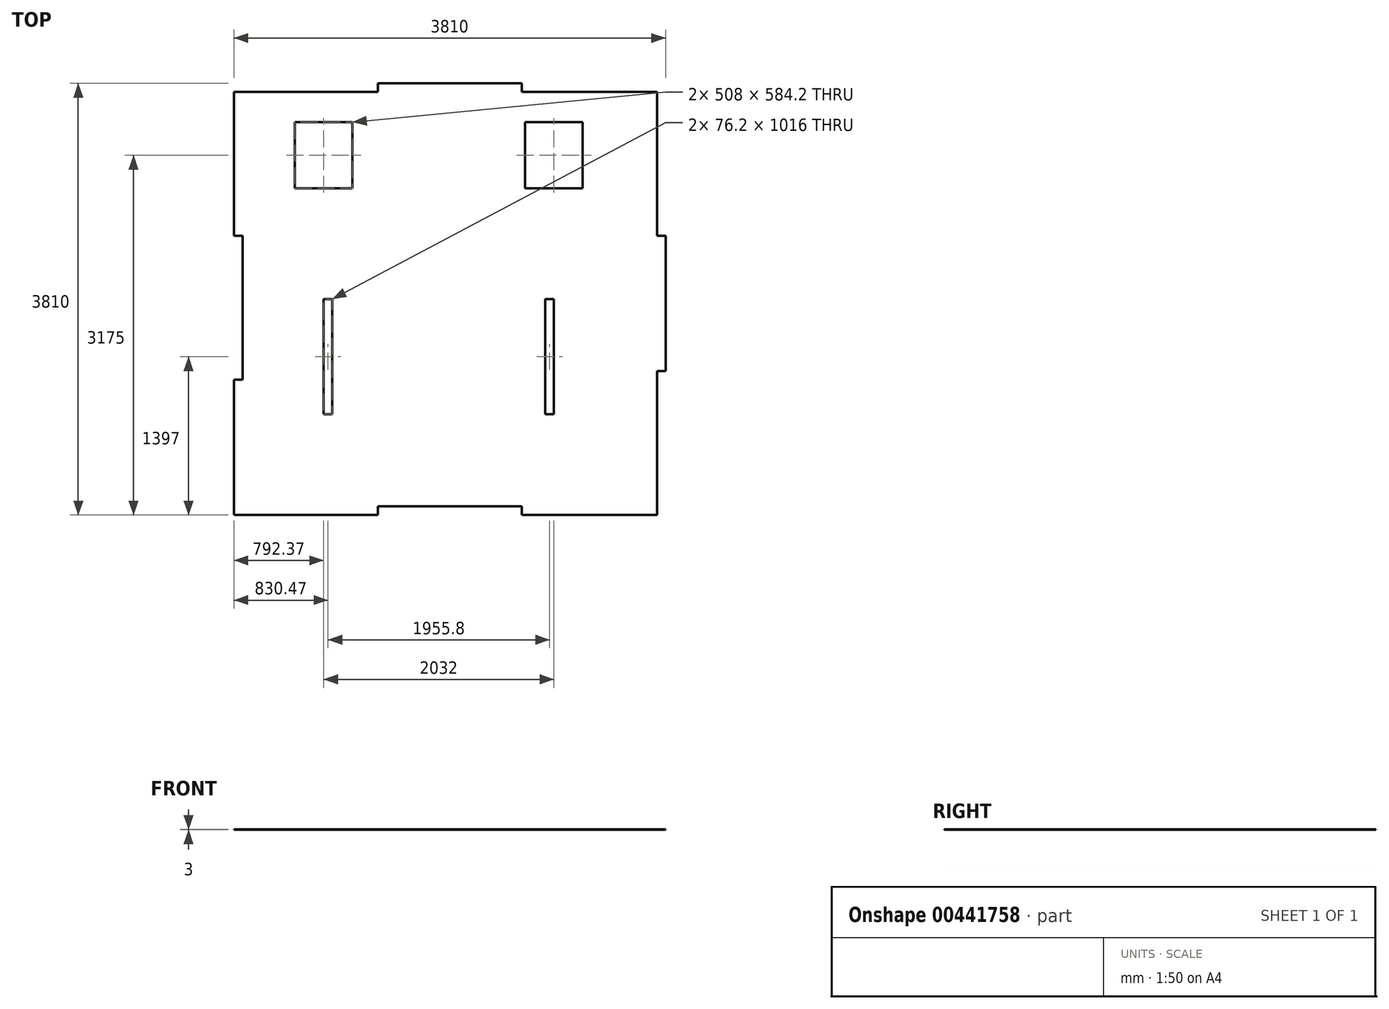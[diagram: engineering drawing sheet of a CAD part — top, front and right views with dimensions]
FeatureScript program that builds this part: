
annotation { "Feature Type Name" : "Feature", "Feature Type Description" : "" }
export const myFeature = defineFeature(function(context is Context, id is Id, definition is map)
    precondition{}
    {
        {
            var Q0;
            Q0=qCreatedBy(makeId("Top.planeOp"),FACE);
            var sketch = newSketch(context, id + "F0", { "sketchPlane" : qUnion([Q0])});
            skLineSegment(sketch, "E0.bottom", {"start": v(731.63, 1905) * mm, "end": v(-538.37, 1905) * mm});
            skLineSegment(sketch, "E0.top", {"start": v(1925.43, -1905) * mm, "end": v(731.63, -1905) * mm});
            skLineSegment(sketch, "E0.left", {"start": v(2001.63, 558.8) * mm, "end": v(2001.63, -635) * mm});
            skLineSegment(sketch, "E0.right", {"start": v(-1808.37, 1828.8) * mm, "end": v(-1808.37, 558.8) * mm});
            skPoint(sketch, "E0.middle", {"position": v(96.63, 0) * mm});
            skLineSegment(sketch, "E1", {"start": v(-1808.37, 1828.8) * mm, "end": v(-538.37, 1828.8) * mm});
            skLineSegment(sketch, "E2", {"start": v(-538.37, 1828.8) * mm, "end": v(-538.37, 1905) * mm});
            skLineSegment(sketch, "E3", {"start": v(1925.43, 1828.8) * mm, "end": v(731.63, 1828.8) * mm});
            skLineSegment(sketch, "E4", {"start": v(731.63, 1828.8) * mm, "end": v(731.63, 1905) * mm});
            skLineSegment(sketch, "E5", {"start": v(-1808.37, -1905) * mm, "end": v(-538.37, -1905) * mm});
            skLineSegment(sketch, "E6", {"start": v(-538.37, -1905) * mm, "end": v(-538.37, -1828.8) * mm});
            skLineSegment(sketch, "E7", {"start": v(-538.37, -1828.8) * mm, "end": v(731.63, -1828.8) * mm});
            skLineSegment(sketch, "E8", {"start": v(731.63, -1828.8) * mm, "end": v(731.63, -1905) * mm});
            skLineSegment(sketch, "E9.trimOffspring", {"start": v(-538.37, -1905) * mm, "end": v(-1808.37, -1905) * mm});
            skPoint(sketch, "E10.orphan", {"position": v(-1808.37, 1905) * mm});
            skPoint(sketch, "E11.orphan", {"position": v(2001.63, 1905) * mm});
            skLineSegment(sketch, "E12", {"start": v(-1808.37, 558.8) * mm, "end": v(-1732.17, 558.8) * mm});
            skLineSegment(sketch, "E13", {"start": v(-1732.17, 558.8) * mm, "end": v(-1732.17, -711.2) * mm});
            skLineSegment(sketch, "E14", {"start": v(-1732.17, -711.2) * mm, "end": v(-1808.37, -711.2) * mm});
            skLineSegment(sketch, "E15.trimOffspring", {"start": v(-1808.37, -711.2) * mm, "end": v(-1808.37, -1905) * mm});
            skLineSegment(sketch, "E16", {"start": v(1925.43, -1905) * mm, "end": v(1925.43, -635) * mm});
            skLineSegment(sketch, "E17", {"start": v(1925.43, -635) * mm, "end": v(2001.63, -635) * mm});
            skPoint(sketch, "E18.orphan", {"position": v(2001.63, -1905) * mm});
            skLineSegment(sketch, "E19", {"start": v(1925.43, 558.8) * mm, "end": v(2001.63, 558.8) * mm});
            skLineSegment(sketch, "E20", {"start": v(1925.43, 558.8) * mm, "end": v(1925.43, 1828.8) * mm});
            skLineSegment(sketch, "E21.bottom", {"start": v(-939.8, 0) * mm, "end": v(-1016, 0) * mm});
            skLineSegment(sketch, "E21.top", {"start": v(-939.8, -1016) * mm, "end": v(-1016, -1016) * mm});
            skLineSegment(sketch, "E21.right", {"start": v(-1016, 0) * mm, "end": v(-1016, -1016) * mm});
            skLineSegment(sketch, "E22.top", {"start": v(939.8, -1016) * mm, "end": v(1016, -1016) * mm});
            skLineSegment(sketch, "E22.right", {"start": v(1016, 0) * mm, "end": v(1016, -1016) * mm});
            skLineSegment(sketch, "E23", {"start": v(-1016, 0) * mm, "end": v(-939.8, 0) * mm});
            skLineSegment(sketch, "E24", {"start": v(-939.8, 0) * mm, "end": v(-939.8, -1016) * mm});
            skLineSegment(sketch, "E25", {"start": v(1016, 0) * mm, "end": v(939.8, 0) * mm});
            skLineSegment(sketch, "E26", {"start": v(939.8, 0) * mm, "end": v(939.8, -1016) * mm});
            skLineSegment(sketch, "E27.trimOffspring", {"start": v(939.8, 0) * mm, "end": v(1016, 0) * mm});
            skPoint(sketch, "E28.start.orphan", {"position": v(0, -1016) * mm});
            skLineSegment(sketch, "E29.bottom", {"start": v(-1270, 977.9) * mm, "end": v(-762, 977.9) * mm});
            skLineSegment(sketch, "E29.top", {"start": v(-1270, 1562.1) * mm, "end": v(-762, 1562.1) * mm});
            skLineSegment(sketch, "E29.left", {"start": v(-1270, 977.9) * mm, "end": v(-1270, 1562.1) * mm});
            skLineSegment(sketch, "E29.right", {"start": v(-762, 977.9) * mm, "end": v(-762, 1562.1) * mm});
            skPoint(sketch, "E29.middle", {"position": v(-1016, 1270) * mm});
            skLineSegment(sketch, "E30.bottom", {"start": v(1270, 1562.1) * mm, "end": v(762, 1562.1) * mm});
            skLineSegment(sketch, "E30.top", {"start": v(1270, 977.9) * mm, "end": v(762, 977.9) * mm});
            skLineSegment(sketch, "E30.left", {"start": v(1270, 1562.1) * mm, "end": v(1270, 977.9) * mm});
            skLineSegment(sketch, "E30.right", {"start": v(762, 1562.1) * mm, "end": v(762, 977.9) * mm});
            skPoint(sketch, "E30.middle", {"position": v(1016, 1270) * mm});
            skSolve(sketch);
        }
        {
            var Q0;
            Q0 = qSketchRegion(id + "F0", true);
            extrude(context, id + "F1", {"entities" : qUnion([Q0]), "depth" : 3 * mm});
        }
    });
